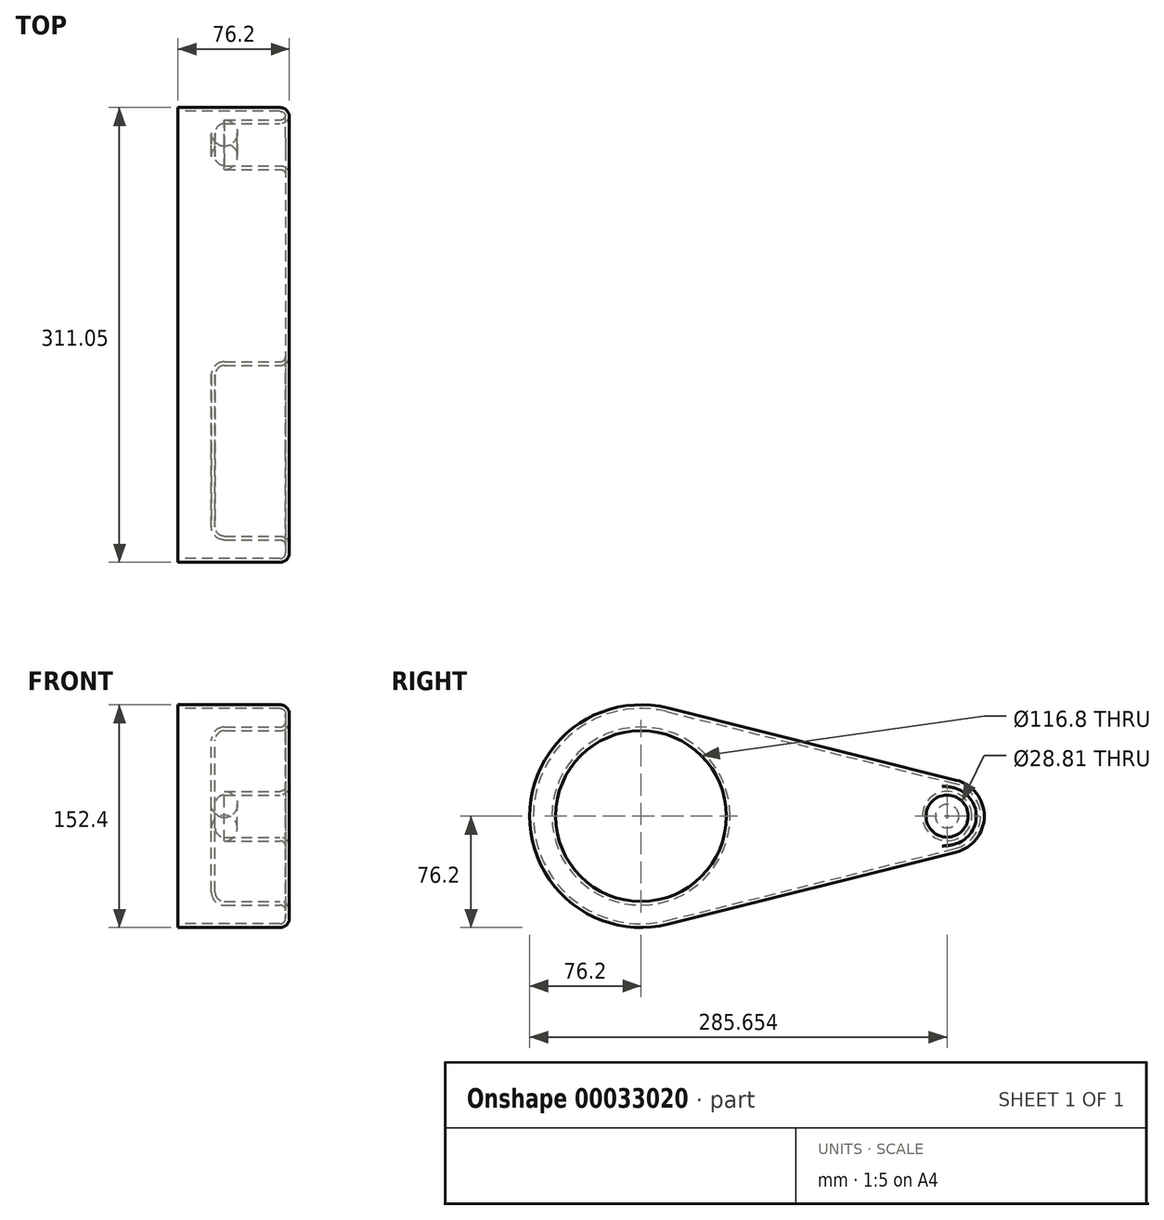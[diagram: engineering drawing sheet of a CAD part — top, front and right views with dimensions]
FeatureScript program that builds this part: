
annotation { "Feature Type Name" : "Feature", "Feature Type Description" : "" }
export const myFeature = defineFeature(function(context is Context, id is Id, definition is map)
    precondition{}
    {
        {
            var Q0;
            Q0=qCreatedBy(makeId("Right.planeOp"),FACE);
            var sketch = newSketch(context, id + "F5", { "sketchPlane" : qUnion([Q0])});
            skCircle(sketch, "E0", {"center": v(0, 0) * mm, "radius": 76.2 * mm});
            skCircle(sketch, "E1", {"center": v(209.45, 0) * mm, "radius": 25.4 * mm});
            skLineSegment(sketch, "E2", {"start": v(18.48, 73.92) * mm, "end": v(215.61, 24.64) * mm});
            skLineSegment(sketch, "E3", {"start": v(18.48, -73.92) * mm, "end": v(215.61, -24.64) * mm});
            skSolve(sketch);
        }
        {
            var Q0;
            {var subQ1=sQuery(id+"F5.wireOp",EDGE,"E2");Q0=makeQuery(id+"F5.imprint","IMPRINT",FACE,{"disambiguationData":[TD([[makeQuery(id+"F5.imprint","IMPRINT",EDGE,{"derivedFrom":subQ1}),-1.0]])]});}
            var sketch = newSketch(context, id + "F0", { "sketchPlane" : qUnion([Q0])});
            skSolve(sketch);
        }
        {
            var Q0;
            Q0 = qSketchRegion(id + "F0", true);
            var Q1;
            {var subQ1=sQuery(id+"F5.wireOp",EDGE,"E2");Q1=makeQuery(id+"F5.imprint","IMPRINT",FACE,{"disambiguationData":[TD([[makeQuery(id+"F5.imprint","IMPRINT",EDGE,{"derivedFrom":subQ1}),-1.0]])]});}
            var Q2;
            {var subQ0=sQuery(id+"F5.wireOp",EDGE,"E0");var subQ2=makeQuery(id+"F5.imprint","INTERSECT",VERTEX,{"derivedFrom":[subQ0,sQuery(id+"F5.wireOp",EDGE,"E2")]});Q2=makeQuery(id+"F5.imprint","IMPRINT",FACE,{"disambiguationData":[TD([[makeQuery(id+"F5.imprint","IMPRINT",EDGE,{"disambiguationData":[TD([[subQ2,-1.0]])],"derivedFrom":subQ0}),1.0]])]});}
            var Q3;
            {var subQ0=sQuery(id+"F5.wireOp",EDGE,"E1");var subQ2=makeQuery(id+"F5.imprint","INTERSECT",VERTEX,{"derivedFrom":[subQ0,sQuery(id+"F5.wireOp",EDGE,"E2")]});Q3=makeQuery(id+"F5.imprint","IMPRINT",FACE,{"disambiguationData":[TD([[makeQuery(id+"F5.imprint","IMPRINT",EDGE,{"disambiguationData":[TD([[subQ2,-1.0]])],"derivedFrom":subQ0}),1.0]])]});}
            extrude(context, id + "F1", {"entities" : qUnion([Q0, Q1, Q2, Q3]), "depth" : 76.2 * mm});
        }
        {
            var Q0;
            Q0=makeQuery(id+"F1.opExtrude","CAP_FACE",FACE,{"disambiguationData":[OSD([sQuery(id+"F5.wireOp",EDGE,"E0"),sQuery(id+"F5.wireOp",EDGE,"E1"),sQuery(id+"F5.wireOp",EDGE,"E2"),sQuery(id+"F5.wireOp",EDGE,"E3")])],"isStart":false});
            var sketch = newSketch(context, id + "F2", { "sketchPlane" : qUnion([Q0])});
            skCircle(sketch, "E4", {"center": v(209.45, 0) * mm, "radius": 14.4 * mm});
            skCircle(sketch, "E5", {"center": v(0, 0) * mm, "radius": 58.4 * mm});
            skSolve(sketch);
        }
        {
            var Q0;
            Q0=makeQuery(id+"F2.imprint","IMPRINT",FACE,{"disambiguationData":[TD([[makeQuery(id+"F2.imprint","IMPRINT",EDGE,{"derivedFrom":sQuery(id+"F2.wireOp",EDGE,"E5")}),1.0]])]});
            var Q1;
            Q1=makeQuery(id+"F2.imprint","IMPRINT",FACE,{"disambiguationData":[TD([[makeQuery(id+"F2.imprint","IMPRINT",EDGE,{"derivedFrom":sQuery(id+"F2.wireOp",EDGE,"E4")}),1.0]])]});
            extrude(context, id + "F6", {"entities" : qUnion([Q0, Q1]), "operationType" : NewBodyOperationType.REMOVE, "oppositeDirection" : true, "depth" : 50.8 * mm});
        }
        {
            var Q0;
            Q0=makeQuery(id+"F1.opExtrude","CAP_FACE",FACE,{"disambiguationData":[OSD([sQuery(id+"F5.wireOp",EDGE,"E0"),sQuery(id+"F5.wireOp",EDGE,"E1"),sQuery(id+"F5.wireOp",EDGE,"E2"),sQuery(id+"F5.wireOp",EDGE,"E3")])],"isStart":false});
            var Q1;
            Q1=makeQuery(id+"F6.boolean.opBoolean","COPY",FACE,{"derivedFrom":makeQuery(id+"F6.opExtrude","CAP_FACE",FACE,{"disambiguationData":[OSD([sQuery(id+"F2.wireOp",EDGE,"E5")])],"isStart":false})});
            var Q2;
            Q2=makeQuery(id+"F6.boolean.opBoolean","COPY",FACE,{"derivedFrom":makeQuery(id+"F6.opExtrude","CAP_FACE",FACE,{"disambiguationData":[OSD([sQuery(id+"F2.wireOp",EDGE,"E4")])],"isStart":false})});
            fillet(context, id + "F3", {"entities" : qUnion([Q0, Q1, Q2]), "radius" : 6.35 * mm, "tangentPropagation" : true, "allowEdgeOverflow" : false});
        }
        {
            var Q0;
            Q0=makeQuery(id+"F1.opExtrude","CAP_FACE",FACE,{"disambiguationData":[OSD([sQuery(id+"F5.wireOp",EDGE,"E0"),sQuery(id+"F5.wireOp",EDGE,"E1"),sQuery(id+"F5.wireOp",EDGE,"E2"),sQuery(id+"F5.wireOp",EDGE,"E3")])],"isStart":true});
            shell(context, id + "F4", {"entities" : qUnion([Q0]), "thickness" : 2.54 * mm});
        }
    });
